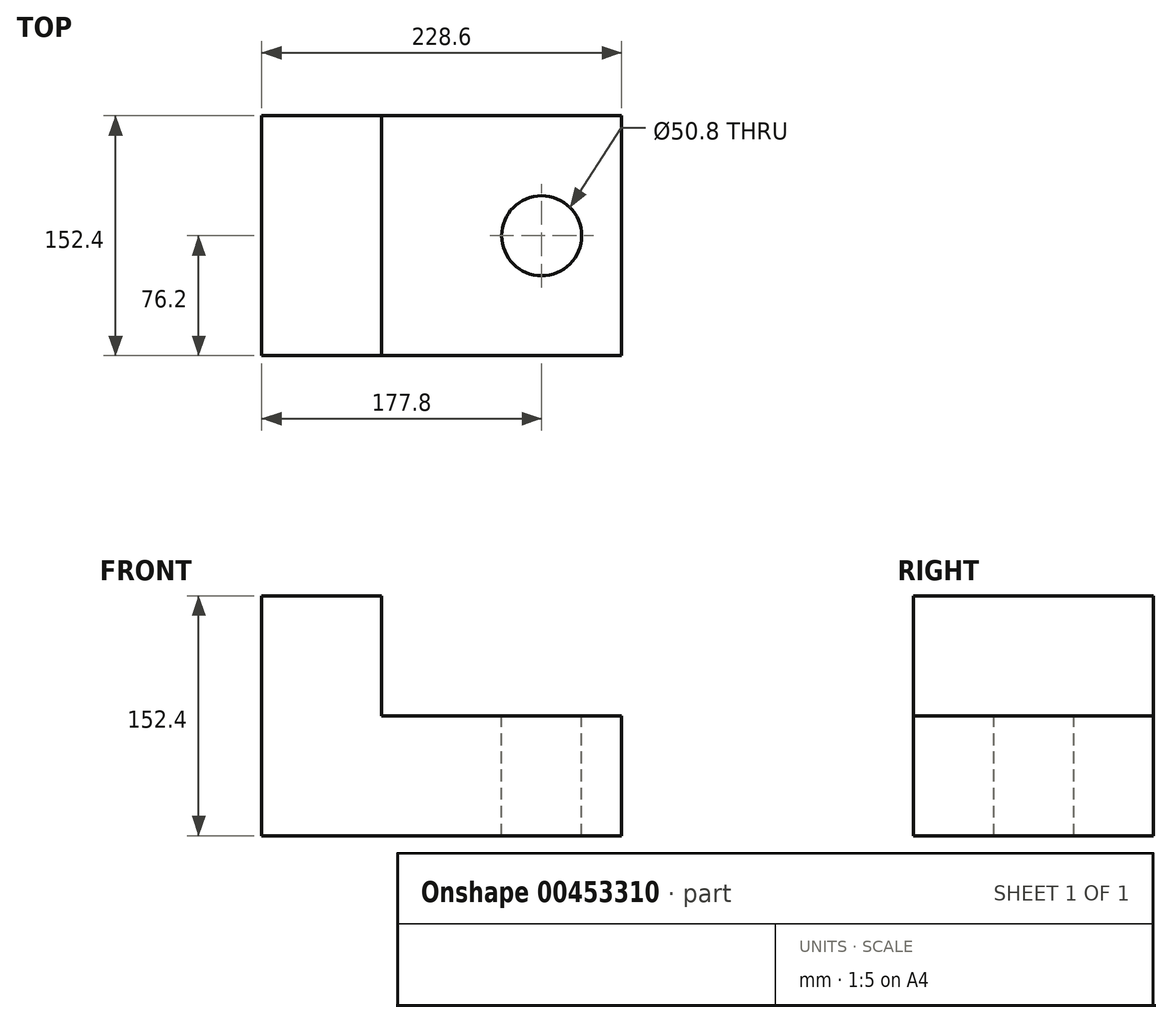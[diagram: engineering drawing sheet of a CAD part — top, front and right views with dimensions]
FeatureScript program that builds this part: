
annotation { "Feature Type Name" : "Feature", "Feature Type Description" : "" }
export const myFeature = defineFeature(function(context is Context, id is Id, definition is map)
    precondition{}
    {
        {
            var Q0;
            Q0=qCreatedBy(makeId("Front.planeOp"),FACE);
            var sketch = newSketch(context, id + "F0", { "sketchPlane" : qUnion([Q0])});
            skLineSegment(sketch, "E0", {"start": v(114.3, -76.2) * mm, "end": v(-114.3, -76.2) * mm});
            skLineSegment(sketch, "E1", {"start": v(-114.3, -76.2) * mm, "end": v(-114.3, 76.2) * mm});
            skLineSegment(sketch, "E2.MirrorCS", {"start": v(114.3, 76.2) * mm, "end": v(-114.3, 76.2) * mm});
            skLineSegment(sketch, "E3.MirrorCS", {"start": v(114.3, -76.2) * mm, "end": v(114.3, 76.2) * mm});
            skSolve(sketch);
        }
        {
            var Q0;
            Q0=makeQuery(id+"F0.imprint","IMPRINT",FACE,{"disambiguationData":[TD([[makeQuery(id+"F0.imprint","IMPRINT",EDGE,{"derivedFrom":sQuery(id+"F0.wireOp",EDGE,"E0")}),-1.0]])]});
            extrude(context, id + "F1", {"entities" : qUnion([Q0]), "endBound" : BoundingType.SYMMETRIC, "depth" : 152.4 * mm});
        }
        {
            var Q0;
            Q0=makeQuery(id+"F1.opExtrude","CAP_FACE",FACE,{"disambiguationData":[OSD([sQuery(id+"F0.wireOp",EDGE,"E0"),sQuery(id+"F0.wireOp",EDGE,"E1"),sQuery(id+"F0.wireOp",EDGE,"E2.MirrorCS"),sQuery(id+"F0.wireOp",EDGE,"E3.MirrorCS")])],"isStart":false});
            var sketch = newSketch(context, id + "F2", { "sketchPlane" : qUnion([Q0])});
            skLineSegment(sketch, "E4", {"start": v(114.3, 76.2) * mm, "end": v(-38.1, 76.2) * mm});
            skLineSegment(sketch, "E5", {"start": v(-38.1, 76.2) * mm, "end": v(-38.1, 0) * mm});
            skLineSegment(sketch, "E6", {"start": v(-38.1, 0) * mm, "end": v(114.3, 0) * mm});
            skLineSegment(sketch, "E7", {"start": v(114.3, 0) * mm, "end": v(114.3, 76.2) * mm});
            skSolve(sketch);
        }
        {
            var Q0;
            Q0=makeQuery(id+"F2.imprint","IMPRINT",FACE,{"disambiguationData":[TD([[makeQuery(id+"F2.imprint","IMPRINT",EDGE,{"derivedFrom":sQuery(id+"F2.wireOp",EDGE,"E4")}),1.0]])]});
            extrude(context, id + "F3", {"entities" : qUnion([Q0]), "operationType" : NewBodyOperationType.REMOVE, "endBound" : BoundingType.THROUGH_ALL, "oppositeDirection" : true, "depth" : 25.4 * mm});
        }
        {
            var Q0;
            Q0=makeQuery(id+"F3.boolean.opBoolean","COPY",FACE,{"derivedFrom":makeQuery(id+"F3.opExtrude","SWEPT_FACE",FACE,{"disambiguationData":[OSD([sQuery(id+"F2.wireOp",EDGE,"E6")])]})});
            var sketch = newSketch(context, id + "F4", { "sketchPlane" : qUnion([Q0])});
            skPoint(sketch, "E8", {"position": v(63.5, 0) * mm});
            skSolve(sketch);
        }
        {
            var Q0;
            Q0=sQuery(id+"F4.wireOp",VERTEX,"E8");
            var Q1;
            Q1=makeQuery(id+"F1.opExtrude","SWEPT_BODY",BODY,{"disambiguationData":[OSD([sQuery(id+"F0.wireOp",EDGE,"E0"),sQuery(id+"F0.wireOp",EDGE,"E1"),sQuery(id+"F0.wireOp",EDGE,"E2.MirrorCS"),sQuery(id+"F0.wireOp",EDGE,"E3.MirrorCS")])]});
            hole(context, id + "F5", {"style" : HoleStyle.SIMPLE, "endStyle" : HoleEndStyle.THROUGH, "holeDiameter" : 50.8 * mm, "isTappedThrough" : true, "tappedDepth" : 12.7 * mm, "tapClearance" : 3, "locations" : qUnion([Q0]), "scope" : qUnion([Q1])});
        }
    });
